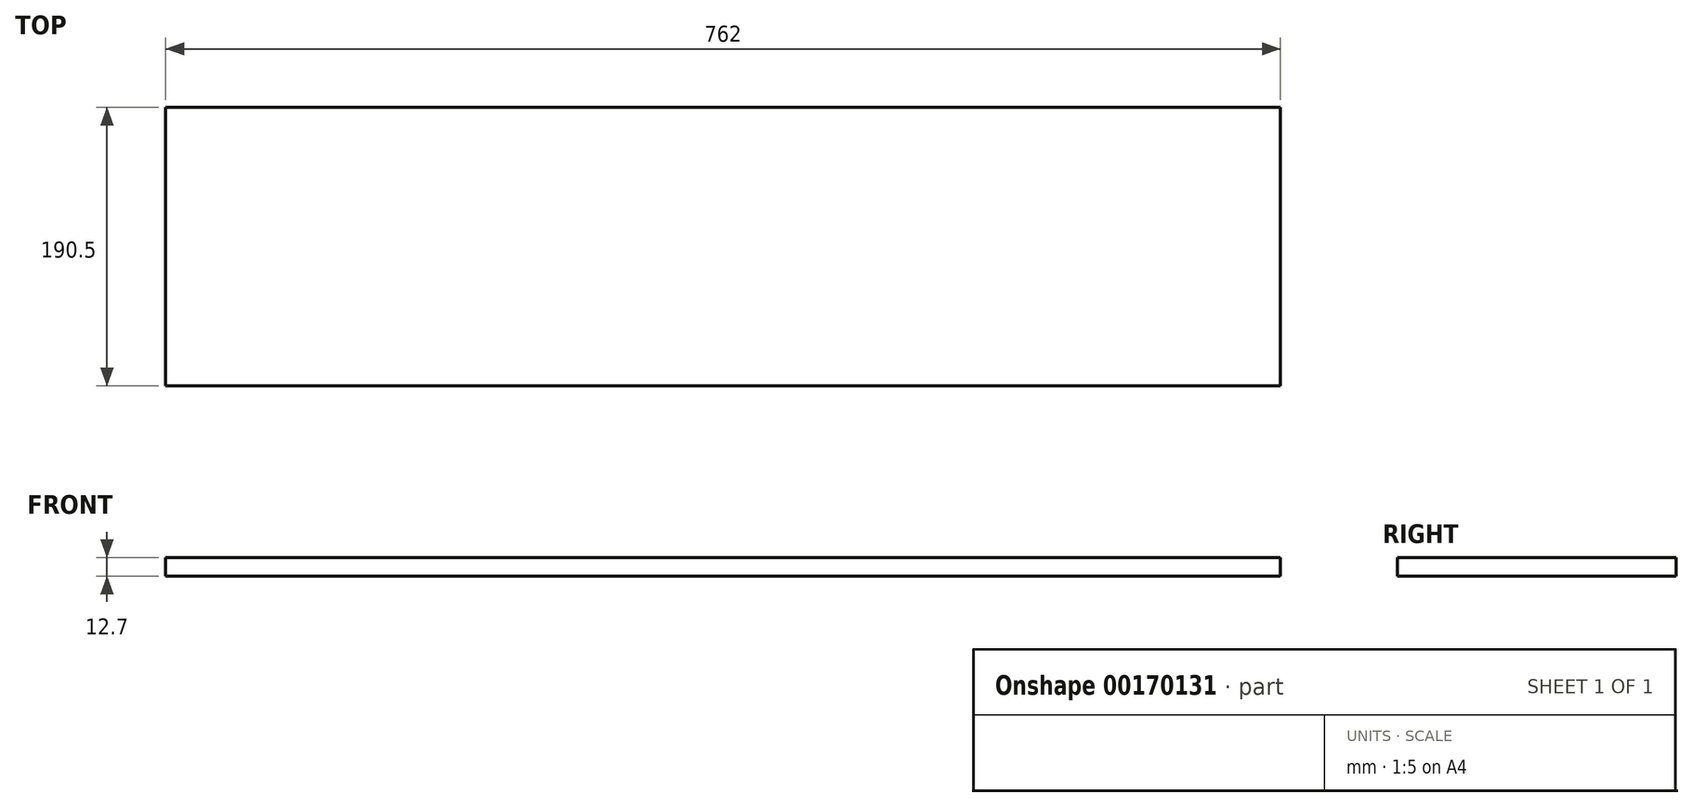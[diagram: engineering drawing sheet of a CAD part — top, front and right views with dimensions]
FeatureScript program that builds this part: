
annotation { "Feature Type Name" : "Feature", "Feature Type Description" : "" }
export const myFeature = defineFeature(function(context is Context, id is Id, definition is map)
    precondition{}
    {
        {
            var Q0;
            Q0=qCreatedBy(makeId("Front.planeOp"),FACE);
            var sketch = newSketch(context, id + "F0", { "sketchPlane" : qUnion([Q0])});
            skLineSegment(sketch, "E0.bottom", {"start": v(0, 0) * mm, "end": v(762, 0) * mm});
            skLineSegment(sketch, "E0.top", {"start": v(0, 12.7) * mm, "end": v(762, 12.7) * mm});
            skLineSegment(sketch, "E0.left", {"start": v(0, 0) * mm, "end": v(0, 12.7) * mm});
            skLineSegment(sketch, "E0.right", {"start": v(762, 0) * mm, "end": v(762, 12.7) * mm});
            skSolve(sketch);
        }
        {
            var Q0;
            Q0 = qSketchRegion(id + "F0", true);
            extrude(context, id + "F1", {"entities" : qUnion([Q0]), "depth" : 190.5 * mm});
        }
    });
